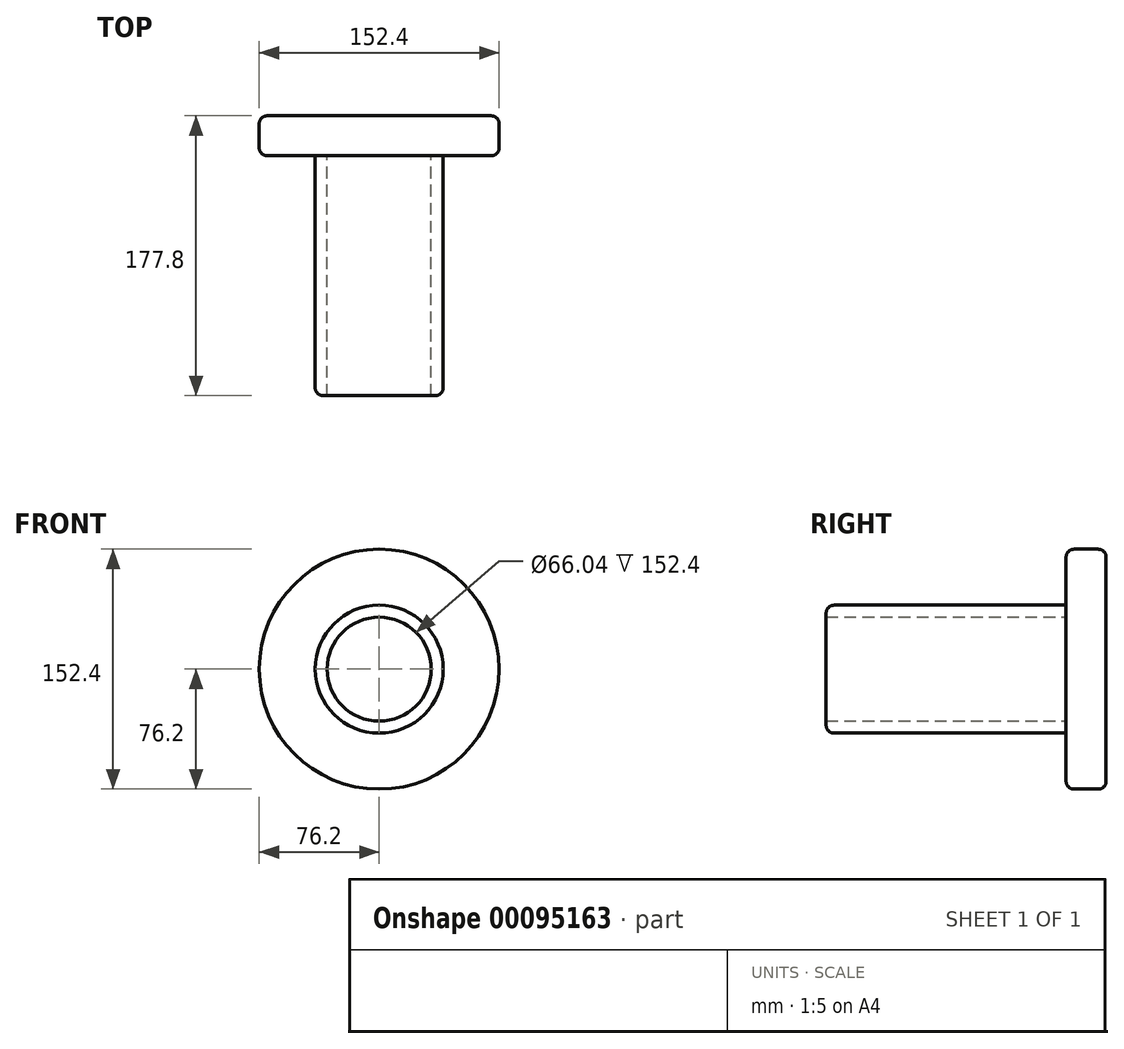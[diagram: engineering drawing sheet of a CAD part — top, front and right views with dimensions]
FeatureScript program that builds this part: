
annotation { "Feature Type Name" : "Feature", "Feature Type Description" : "" }
export const myFeature = defineFeature(function(context is Context, id is Id, definition is map)
    precondition{}
    {
        {
            var Q0;
            Q0=qCreatedBy(makeId("Front.planeOp"),FACE);
            var sketch = newSketch(context, id + "F0", { "sketchPlane" : qUnion([Q0])});
            skCircle(sketch, "E0", {"center": v(0, 0) * mm, "radius": 40.64 * mm});
            skCircle(sketch, "E1.0", {"center": v(0, 0) * mm, "radius": 33.02 * mm});
            skSolve(sketch);
        }
        {
            var Q0;
            Q0 = qSketchRegion(id + "F0", true);
            extrude(context, id + "F1", {"entities" : qUnion([Q0]), "depth" : 152.4 * mm});
        }
        {
            var Q0;
            Q0=qCreatedBy(makeId("Front.planeOp"),FACE);
            var sketch = newSketch(context, id + "F2", { "sketchPlane" : qUnion([Q0])});
            skCircle(sketch, "E2", {"center": v(0, 0) * mm, "radius": 76.2 * mm});
            skSolve(sketch);
        }
        {
            var Q0;
            Q0=makeQuery(id+"F2.imprint","IMPRINT",FACE,{"disambiguationData":[TD([[makeQuery(id+"F2.imprint","IMPRINT",EDGE,{"derivedFrom":sQuery(id+"F2.wireOp",EDGE,"E2")}),1.0]])]});
            extrude(context, id + "F3", {"entities" : qUnion([Q0]), "operationType" : NewBodyOperationType.ADD, "oppositeDirection" : true, "depth" : 25.4 * mm});
        }
        {
            var Q0;
            Q0=makeQuery(id+"F3.opExtrude","SWEPT_FACE",FACE,{"disambiguationData":[OSD([sQuery(id+"F2.wireOp",EDGE,"E2")])]});
            fillet(context, id + "F4", {"entities" : qUnion([Q0]), "radius" : 5.08 * mm, "tangentPropagation" : true, "allowEdgeOverflow" : false});
        }
        {
            var Q0;
            Q0=makeQuery(id+"F1.opExtrude","CAP_EDGE",EDGE,{"disambiguationData":[OSD([sQuery(id+"F0.wireOp",EDGE,"E0")])],"isStart":false});
            fillet(context, id + "F5", {"entities" : qUnion([Q0]), "radius" : 5.08 * mm, "tangentPropagation" : true, "allowEdgeOverflow" : false});
        }
    });
